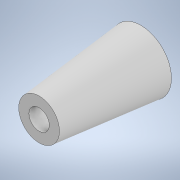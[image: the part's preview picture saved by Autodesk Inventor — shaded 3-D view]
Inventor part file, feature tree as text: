
AUTODESK INVENTOR PART (.ipt)
format: ipt  version: 2022 (Build 260153000, 153)  size: 114,688 bytes
history: native  units: mm
features: sketch x4, extrude x2, plane x1, loft x1
ambient origin geometry x8: Origin, YZ Plane, XZ Plane, XY Plane, X Axis, Y Axis, Z Axis, Center Point
bodies: Solid1 (feature_tree)
feature tree (8):
  sketch  "Sketch1"  dims[d0=30.0mm d1=50.0mm]
  plane  "Work Plane1"
  loft  "Loft1"
  extrude  "Extrusion1"  TaperAngle=0.0deg  [1 undecoded]
  extrude  "Extrusion2"  Depth=10.0mm
  sketch  "Sketch2"  dims[d2=20.0mm d3=0.0mm d4=90.0deg]
  sketch  "Sketch3"  dims[d5=0.0mm d6=90.0deg d7=10.0mm]
  sketch  "Sketch4"  dims[d8=47.0mm d9=0.0mm d10=3.5mm d11=10.0mm d12=0.0mm]
note: 1 required parameter value undecoded (feature->parameter linkage not recoverable at this tier; creation-order binding heuristic only, values carry confidence <= 0.55)
